# Revit family: Automatic Revolving Door RD3L
name_source: partatom
category: Doors
units: mm (PartAtom-declared; Revit-internal decimal feet)

## family parameters
Always vertical = Yes
Cut with Voids When Loaded = No
Host = Wall
OmniClass Number = 23.30.10.00
OmniClass Title = Doors
Room Calculation Point = No
Shared = No

## types (4) — shared parameters
Above Panel Height = 1' - 1 1/2"
Above Panel Height Calc = 1' - 1 1/2"
Analytic Construction = <None>
BIMobject QR code url = http://besam.bimobject.com
BIMobject category = Revolving Doors
Date of publishing = 2014-03-28
Depth = 0.00
Depth (mm) = 0' - 0"
Design country = Sweden
Disclaimer = Consult product specification for sensors to comply with ANSI A156.27.
Door Folding = Yes
EAN code = http://-
Edition number = 2
Folding Angle = 32.00°
Frame angle = 31.40°
Function = Interior
HF = 0' - 4 27/32"
HF Calc = 0' - 4 27/32"
HI Calc = 7' - 2 1/2"
HT = 8' - 4"
Height = 7' - 2 1/2"
Height (mm) = 0' - 0"
IFC Classification = Door
Manufacturer = Besam
Manufacturer URL = http://www.besam.co.uk
Manufacturer country = Czech Republic
Manufacturer name = Besam-EMEA
Material main = Aluminium
Material secondary = Glass
Midrail Height = 2' - 9 15/16"
Midrail Option = Yes
Model = RD3L
NBS Reference Code = 25-30-20-70
NBS Reference Description = Revolving Doorset Systems
Nominal height = 0.00
Nominal width = 0.00
Product certification = http://www.assaabloyentrance.com
Product data url = http://besam.bimobject.com
Product family = Automatic Revolving Doors
Product group = Besam Large 3-wing RD3L
Product identifier = besam.bimobject.com/RD3L
QR code = http://besam.bimobject.com
Technical description = http://www.besam.co.uk
UNSPSC Category = Doors
UNSPSC Code = 301715
URL = http://besam.bimobject.com
Uniclass 1.4 Code = L411
Uniclass 1.4 Description = Doors
Uniclass 2.0 Code = SS-25-30-20-70
Uniclass 2.0 Description = Revolving Doorset Systems
Wall Closure = By host
Weight Net (Kg) = 0
Width (mm) = 0' - 0"

## per-type parameters (varying)
| type | Distance | Folding Length | Name of the object | Product SKU | Radius 1 | Radius 2 | Radius 3 | Radous 4 | TW | Width | Wing Length |
| RD700 14' | 6' - 10 15/32" | 4' - 6 9/16" | RD3L | RD3L | 6' - 10 17/32" | 7' - 0 1/2" | 7' - 0 3/32" | 7' - 0 5/32" | 6' - 6 3/8" | 14' - 0 1/2" | 2' - 4 1/16" |
| RD700 16' | 7' - 10 9/32" | 5' - 2 1/16" | RD3L | RD3L | 7' - 10 11/32" | 8' - 0 5/16" | 7' - 11 29/32" | 7' - 11 31/32" | 7' - 6 1/4" | 16' - 0 1/8" | 2' - 8 3/8" |
| RD700 18' | 8' - 10 1/8" | 5' - 9 9/16" | RD700 | RD700 | 8' - 10 3/16" | 9' - 0 5/32" | 8' - 11 3/4" | 8' - 11 13/16" | 8' - 6 1/32" | 17' - 11 25/32" | 3' - 0 23/32" |
| RD700 20' | 10' - 1 27/32" | 6' - 7 9/16" | RD3L | RD3L | 10' - 1 29/32" | 10' - 3 7/8" | 10' - 3 15/32" | 10' - 3 17/32" | 9' - 9 13/16" | 20' - 7 1/4" | 3' - 6 7/16" |

## geometry (parser evidence)
native form markers: Blend x4, Sweep x3
no freeform markers — native parametric forms only
